# Revit family: SHORT SMALL
name_source: partatom
category: Lighting Fixtures
units: mm (PartAtom-declared; Revit-internal decimal feet)

## family parameters
Cut with Voids When Loaded = No
Host = Face
Light Source = Yes
Maintain Annotation Orientation = Yes
Part Type = Normal
Room Calculation Point = No
Round Connector Dimension = Use Diameter
Shared = No

## types (8) — shared parameters
Color Filter = 16777215
Default Elevation = 1219 mm
Dimming Lamp Color Temperature Shift = <None>
Emit from Line Length = 610 mm
LuxLight_Alto = 103 mm
LuxLight_AltoAreaLuminosa = 20 mm
LuxLight_Amperios = 500
LuxLight_Diametro = 80 mm
LuxLight_DiametroAreaLuminosa = 60 mm
LuxLight_Watios = 19 W
Manufacturer = LUXLIGHT
Tilt Angle = 0.00°
zero-valued in all types: LuxLight_Ancho, LuxLight_AnchoAreaLuminosa, LuxLight_Largo, LuxLight_LargoAreaLuminosa, LuxLight_ProtuberanciaTecho

## per-type parameters (varying)
| type | LuxLight_Lumenes | LuxLight_Temperatura | Photometric Web File |
| LXT036S282 | 2115 lm | 2700 K | LXT036S282 .ies |
| LXT036S283 | 2240 lm | 3000 K | LXT036S283 .ies |
| LXT036S235 | 2009 lm | 3500 K | LXT036S235 .ies |
| LXT036S284 | 2370 lm | 4000 K | LXT036S284 .ies |
| LXT036S285 | 2489 lm | 5000 K | LXT036S285 .ies |
| LXT036S293 | 1896 lm | 3000 K | LXT036S293 .ies |
| LXT036S292 | 1659 lm | 2700 K | LXT036S292 .ies |
| LXT036S294 | 2133 lm | 4000 K | LXT036S294 .ies |

## geometry (parser evidence)
native form markers: Sweep x2
no freeform markers — native parametric forms only
